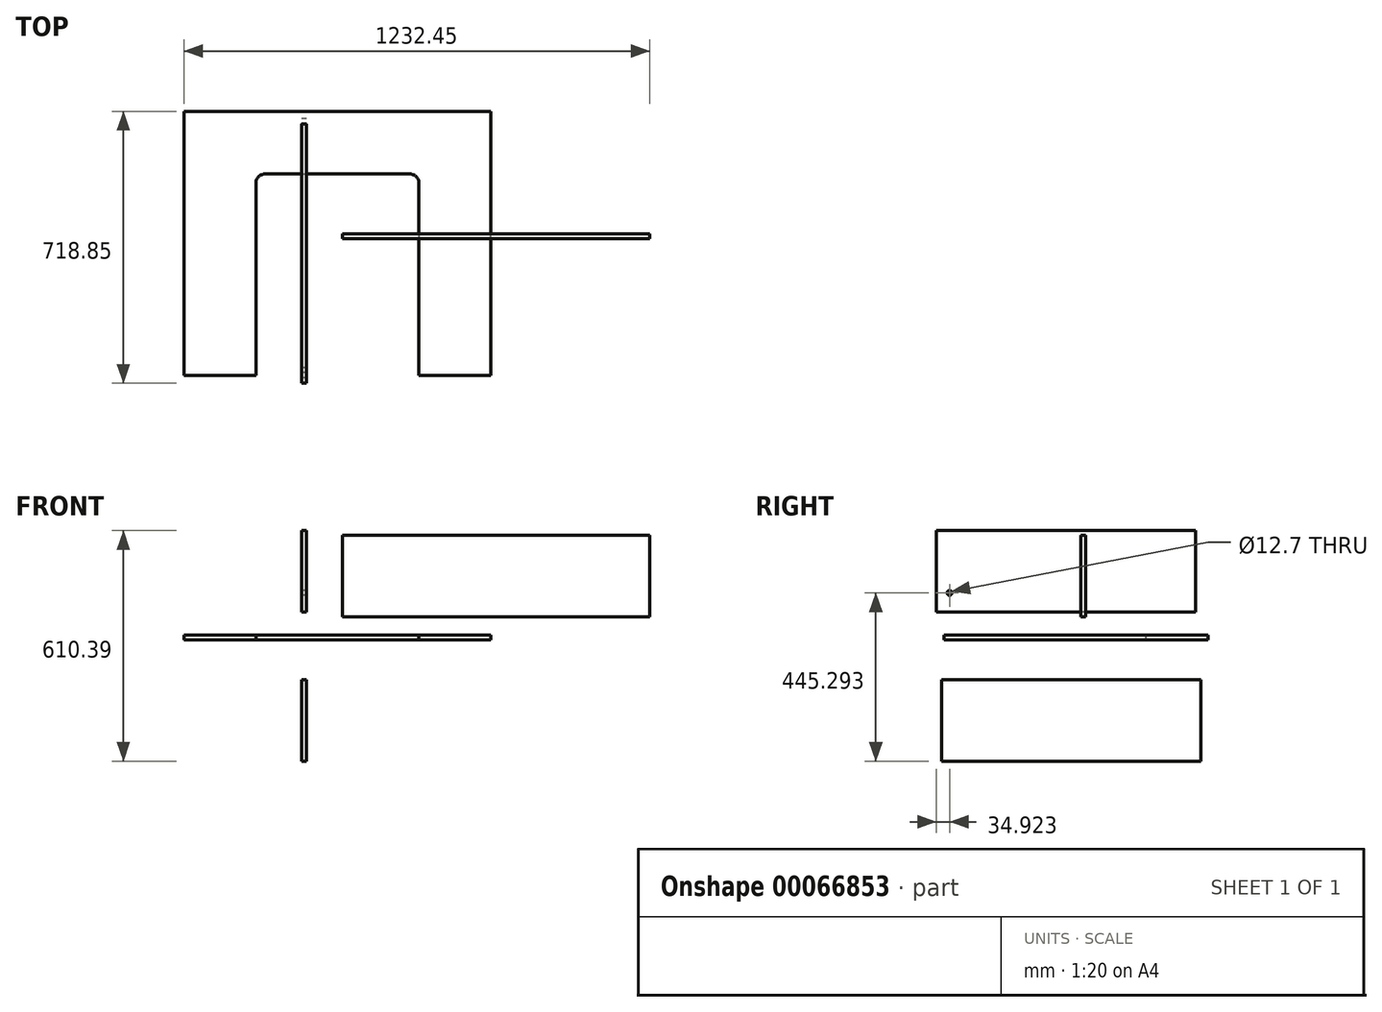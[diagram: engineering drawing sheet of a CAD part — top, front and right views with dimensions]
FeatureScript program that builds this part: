
annotation { "Feature Type Name" : "Feature", "Feature Type Description" : "" }
export const myFeature = defineFeature(function(context is Context, id is Id, definition is map)
    precondition{}
    {
        {
            var Q0;
            Q0=qCreatedBy(makeId("Top.planeOp"),FACE);
            var sketch = newSketch(context, id + "F0", { "sketchPlane" : qUnion([Q0])});
            skLineSegment(sketch, "E0.bottom", {"start": v(-317.7, -368.44) * mm, "end": v(495.1, -368.44) * mm});
            skLineSegment(sketch, "E0.top", {"start": v(-317.7, 330.06) * mm, "end": v(495.1, 330.06) * mm});
            skLineSegment(sketch, "E0.left", {"start": v(-317.7, -368.44) * mm, "end": v(-317.7, 330.06) * mm});
            skLineSegment(sketch, "E0.right", {"start": v(495.1, -368.44) * mm, "end": v(495.1, 330.06) * mm});
            skLineSegment(sketch, "E1", {"start": v(88.7, -368.44) * mm, "end": v(88.7, 612.74) * mm, "construction": true});
            skPoint(sketch, "E1.endSnap0", {"position": v(88.7, 330.06) * mm});
            skLineSegment(sketch, "E2", {"start": v(-376.62, 164.96) * mm, "end": v(348.78, 164.96) * mm, "construction": true});
            skLineSegment(sketch, "E3.bottom", {"start": v(-101.8, 164.96) * mm, "end": v(279.2, 164.96) * mm});
            skLineSegment(sketch, "E3.top", {"start": v(-127.2, -397.31) * mm, "end": v(304.6, -397.31) * mm});
            skLineSegment(sketch, "E3.left", {"start": v(-127.2, 139.56) * mm, "end": v(-127.2, -397.31) * mm});
            skLineSegment(sketch, "E3.right", {"start": v(304.6, 139.56) * mm, "end": v(304.6, -397.31) * mm});
            skArc(sketch, "E4", {"start": v(304.6, 139.56) * mm, "mid": v(297.15, 157.52) * mm, "end": v(279.2, 164.96) * mm});
            skArc(sketch, "E5", {"start": v(-101.8, 164.96) * mm, "mid": v(-119.77, 157.52) * mm, "end": v(-127.2, 139.56) * mm});
            skSolve(sketch);
        }
        {
            var Q0;
            Q0=makeQuery(id+"F0.imprint","IMPRINT",FACE,{"disambiguationData":[TD([[makeQuery(id+"F0.imprint","IMPRINT",EDGE,{"derivedFrom":sQuery(id+"F0.wireOp",EDGE,"E0.bottom")}),1.0]])]});
            extrude(context, id + "F1", {"entities" : qUnion([Q0]), "depth" : 12.7 * mm});
        }
        {
            var Q0;
            Q0=qCreatedBy(makeId("Right.planeOp"),FACE);
            var sketch = newSketch(context, id + "F2", { "sketchPlane" : qUnion([Q0])});
            skLineSegment(sketch, "E6.bottom", {"start": v(297, 73.97) * mm, "end": v(-388.8, 73.97) * mm});
            skLineSegment(sketch, "E6.top", {"start": v(297, 289.87) * mm, "end": v(-388.8, 289.87) * mm});
            skLineSegment(sketch, "E6.left", {"start": v(297, 73.97) * mm, "end": v(297, 289.87) * mm});
            skLineSegment(sketch, "E6.right", {"start": v(-388.8, 73.97) * mm, "end": v(-388.8, 289.87) * mm});
            skCircle(sketch, "E7", {"center": v(-353.87, 124.77) * mm, "radius": 6.35 * mm});
            skSolve(sketch);
        }
        {
            var Q0;
            Q0=makeQuery(id+"F2.imprint","IMPRINT",FACE,{"disambiguationData":[TD([[makeQuery(id+"F2.imprint","IMPRINT",EDGE,{"derivedFrom":sQuery(id+"F2.wireOp",EDGE,"E6.bottom")}),-1.0]])]});
            extrude(context, id + "F3", {"entities" : qUnion([Q0]), "depth" : 12.7 * mm, "symmetric" : true});
        }
        {
            var Q0;
            Q0=qCreatedBy(makeId("Right.planeOp"),FACE);
            var sketch = newSketch(context, id + "F4", { "sketchPlane" : qUnion([Q0])});
            skLineSegment(sketch, "E8.bottom", {"start": v(-374.67, -320.52) * mm, "end": v(311.13, -320.52) * mm});
            skLineSegment(sketch, "E8.top", {"start": v(-374.67, -104.62) * mm, "end": v(311.13, -104.62) * mm});
            skLineSegment(sketch, "E8.left", {"start": v(-374.67, -320.52) * mm, "end": v(-374.67, -104.62) * mm});
            skLineSegment(sketch, "E8.right", {"start": v(311.13, -320.52) * mm, "end": v(311.13, -104.62) * mm});
            skSolve(sketch);
        }
        {
            var Q0;
            Q0=makeQuery(id+"F4.imprint","IMPRINT",FACE,{"disambiguationData":[TD([[makeQuery(id+"F4.imprint","IMPRINT",EDGE,{"derivedFrom":sQuery(id+"F4.wireOp",EDGE,"E8.bottom")}),1.0]])]});
            extrude(context, id + "F5", {"entities" : qUnion([Q0]), "depth" : 12.7 * mm, "symmetric" : true});
        }
        {
            var Q0;
            Q0=qCreatedBy(makeId("Front.planeOp"),FACE);
            var sketch = newSketch(context, id + "F6", { "sketchPlane" : qUnion([Q0])});
            skLineSegment(sketch, "E9.bottom", {"start": v(101.94, 278) * mm, "end": v(914.74, 278) * mm});
            skLineSegment(sketch, "E9.top", {"start": v(101.94, 62.1) * mm, "end": v(914.74, 62.1) * mm});
            skLineSegment(sketch, "E9.left", {"start": v(101.94, 278) * mm, "end": v(101.94, 62.1) * mm});
            skLineSegment(sketch, "E9.right", {"start": v(914.74, 278) * mm, "end": v(914.74, 62.1) * mm});
            skSolve(sketch);
        }
        {
            var Q0;
            Q0=makeQuery(id+"F6.imprint","IMPRINT",FACE,{"disambiguationData":[TD([[makeQuery(id+"F6.imprint","IMPRINT",EDGE,{"derivedFrom":sQuery(id+"F6.wireOp",EDGE,"E9.bottom")}),-1.0]])]});
            extrude(context, id + "F7", {"entities" : qUnion([Q0]), "depth" : 12.7 * mm, "symmetric" : true});
        }
    });
